# Revit family: Sanitary_Accessories_Svedholm_Slits-paper-bin-70l
name_source: partatom
category: Furniture
revit_build: Autodesk Revit 2018 (Build: 20170223_1515(x64)
units: mm (PartAtom-declared; Revit-internal decimal feet)

## family parameters
Cut with Voids When Loaded = No
Host = Face
OmniClass Number = 23.21.11.00
OmniClass Title = Commercial Furniture
Room Calculation Point = No
Shared = No

## types (2) — shared parameters
BIMobject category = Accessories
Default Elevation = 1219 mm
Description = A paper bin with or without lid made of powder coated steel. Adapted for bin liners 600 × 900 mm 70 liters.
Edition number = 1
IFC Classification = Object
Manufacturer = Svedholm
Manufacturer name = Svedholm
Model = Slits paper bin 70l
OmniClass Code = 23-21 11 00
OmniClass Description = Commercial Furniture
Product Guid = a1ee2255-5145-4bf4-8a59-f870a38e49ea
Product SKU = Slits-paper-bin-70l
Product data url = https://bimobject.com
Product family = Slits
Product group = Bin
Product name = Slits paper bin 70l
Product url = https://www.svedholm.se
QR code = https://bimobject.com
URL = https://www.svedholm.se
Uniclass 2015 Code = Zz_30_60
Uniclass 2015 Name = Objects

## per-type parameters (varying)
| type | Paper bin lid |
| ART - (410.600.011) | No |
| ART - (410.600.012) | Yes |

## geometry (parser evidence)
native form markers: Sweep x3
no freeform markers — native parametric forms only
